# Revit family: 2-6114-24 Journey
name_source: partatom
category: Lighting Fixtures
revit_build: Autodesk Revit LT 2014 (Build: 20130308_1515(x64)
units: mm (PartAtom-declared; Revit-internal decimal feet)

## types (1)
- 2-6114-24 Journey
    Apparent Load = 42 VA
    Ballast Manufacturer = Antron Electronics CSS-UV42PS
    Color Filter = 16777215
    Default Elevation = 4' - 0"
    Description = 14" dia. ceiling mount
    Diffuser = White Opal Glass
    Dimming Lamp Color Temperature Shift = <None>
    Emit Shape Visible in Rendering = No
    Emit from Circle Diameter = 2' - 0"
    Fixture Diameter = 1' - 2 1/16"
    Fixture Height = 0' - 4 1/2"
    Input Power (Watts) = 41.6
    Input Voltage (Volts AC) = 120
    Junction Box = 4' Octagonal
    Lamp = 2x26W Double Twin Tube Compact Fluorescent
    Lamp Manufacturer = Sylvania CF26DD/E/830
    Manufacturer = Oxygen Lighting
    Metal Finish = Satin Nickel
    Model = 2-6114-24
    Photometric Web File = 2-6114-24 Journey 14 ITL77197.IES
    Power Factor = 0.99
    Product Documentation Link = http://oxygenlighting.com.s3.amazonaws.com
    Tilt Angle = -90.00°
    Type Comments = Lighting - Fluorescent
    URL = http://www.oxygenlighting.com

## geometry (parser evidence)
native form markers: Sweep x1
no freeform markers — native parametric forms only
